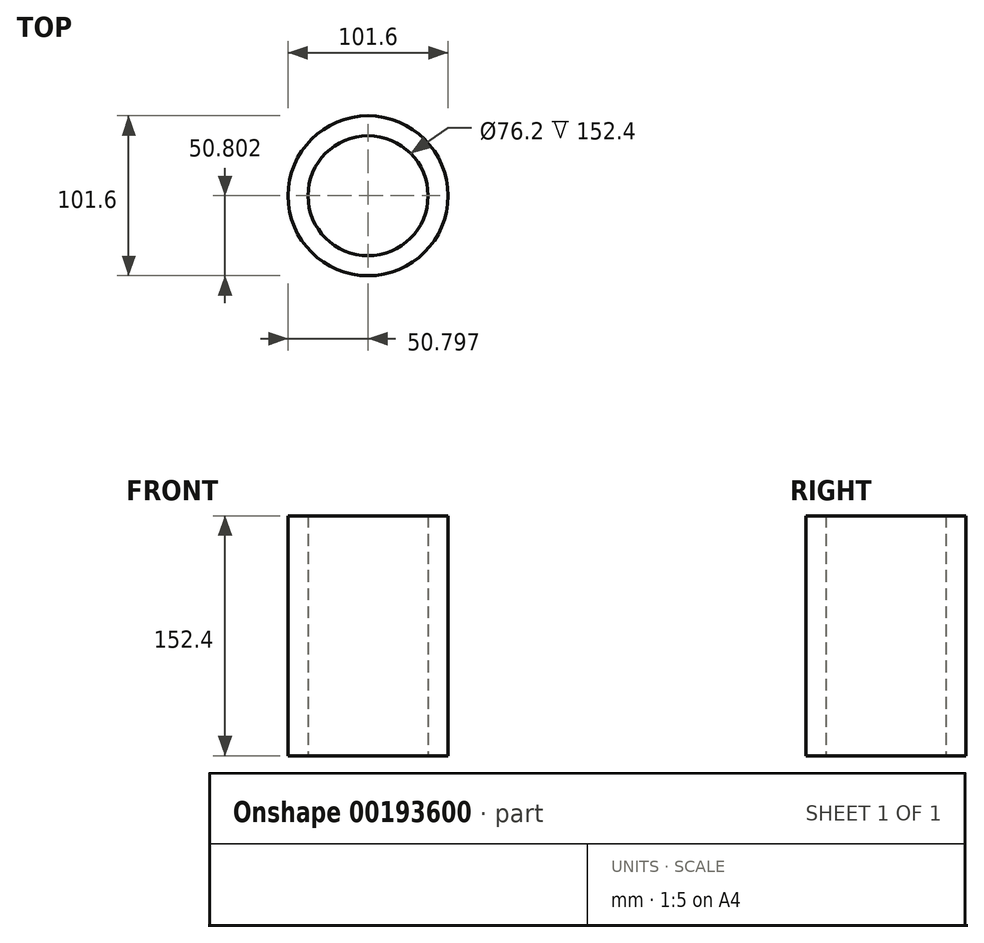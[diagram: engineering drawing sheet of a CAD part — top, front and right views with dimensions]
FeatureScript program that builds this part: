
annotation { "Feature Type Name" : "Feature", "Feature Type Description" : "" }
export const myFeature = defineFeature(function(context is Context, id is Id, definition is map)
    precondition{}
    {
        {
            var Q0;
            Q0=qCreatedBy(makeId("Top.planeOp"),FACE);
            var sketch = newSketch(context, id + "F0", { "sketchPlane" : qUnion([Q0])});
            skCircle(sketch, "E0", {"center": v(11.55, 21.14) * mm, "radius": 50.8 * mm});
            skSolve(sketch);
        }
        {
            var Q0;
            Q0 = qSketchRegion(id + "F0", true);
            extrude(context, id + "F1", {"entities" : qUnion([Q0]), "depth" : 152.4 * mm});
        }
        {
            var Q0;
            Q0=makeQuery(id+"F1.opExtrude","CAP_FACE",FACE,{"disambiguationData":[OSD([sQuery(id+"F0.wireOp",EDGE,"E0")])],"isStart":true});
            var sketch = newSketch(context, id + "F2", { "sketchPlane" : qUnion([Q0])});
            skCircle(sketch, "E1", {"center": v(11.55, -21.14) * mm, "radius": 40.99 * mm});
            skSolve(sketch);
        }
        {
            var Q0;
            Q0=sQuery(id+"F2.wireOp",VERTEX,"E1.center");
            var Q1;
            Q1=makeQuery(id+"F1.opExtrude","SWEPT_BODY",BODY,{"disambiguationData":[OSD([sQuery(id+"F0.wireOp",EDGE,"E0")])]});
            hole(context, id + "F3", {"style" : HoleStyle.SIMPLE, "endStyle" : HoleEndStyle.THROUGH, "holeDiameter" : 76.2 * mm, "locations" : qUnion([Q0]), "scope" : qUnion([Q1]), "isTappedThrough" : true});
        }
    });
